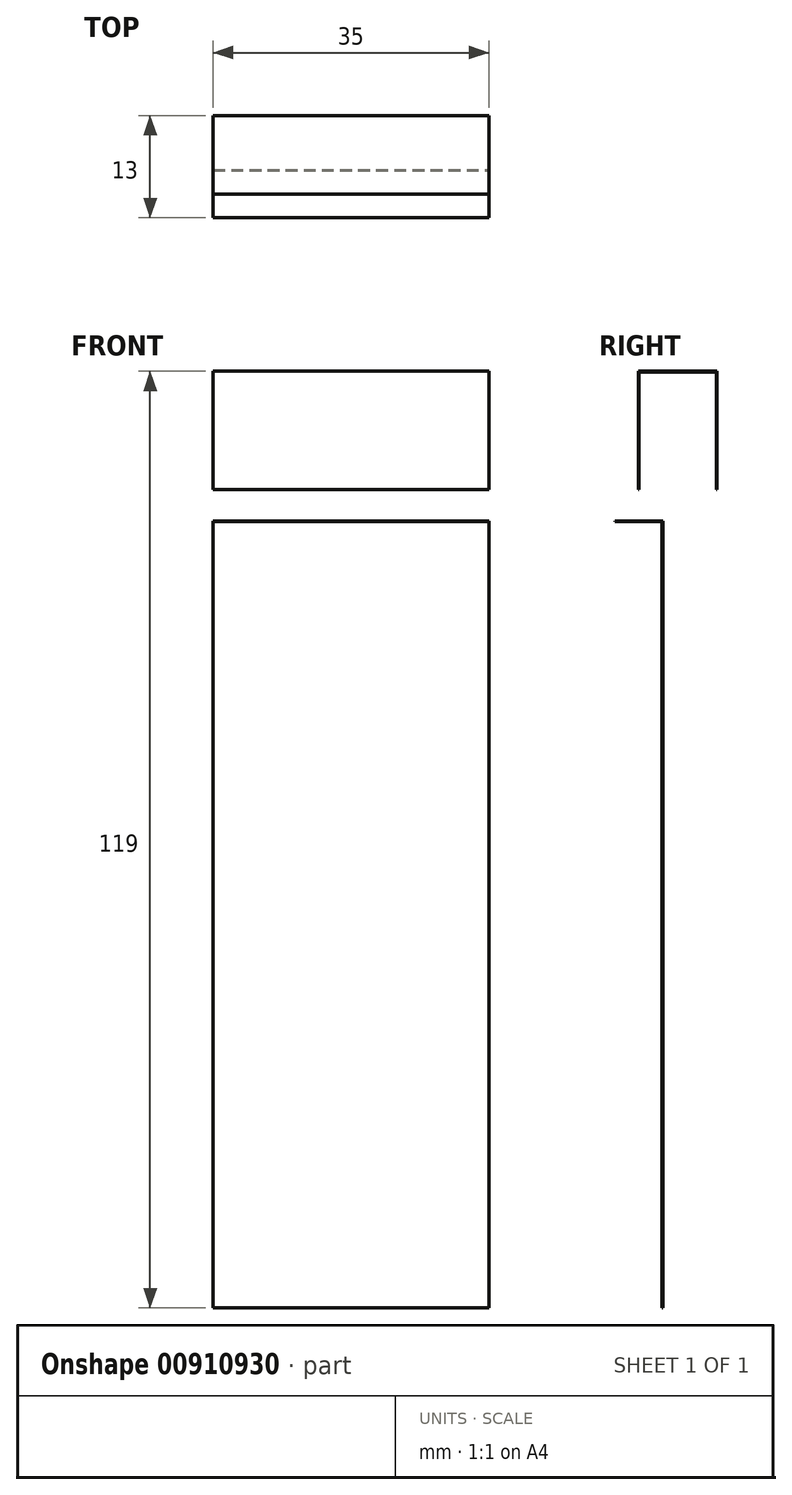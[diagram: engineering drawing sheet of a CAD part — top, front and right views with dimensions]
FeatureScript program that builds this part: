
annotation { "Feature Type Name" : "Feature", "Feature Type Description" : "" }
export const myFeature = defineFeature(function(context is Context, id is Id, definition is map)
    precondition{}
    {
        {
            assignVariable(context, id + "F0", {"name" : "D", "anyValue" : 6});
        }
        {
            assignVariable(context, id + "F1", {"name" : "w", "anyValue" : 35});
        }
        {
            var Q0;
            Q0=qCreatedBy(makeId("Top.planeOp"),FACE);
            var sketch = newSketch(context, id + "F2", { "sketchPlane" : qUnion([Q0])});
            skLineSegment(sketch, "E0.bottom", {"start": v(-17.5, 0.1) * mm, "end": v(17.5, 0.1) * mm});
            skLineSegment(sketch, "E0.top", {"start": v(-17.5, 0) * mm, "end": v(17.5, 0) * mm});
            skLineSegment(sketch, "E0.left", {"start": v(-17.5, 0.1) * mm, "end": v(-17.5, 0) * mm});
            skLineSegment(sketch, "E0.right", {"start": v(17.5, 0.1) * mm, "end": v(17.5, 0) * mm});
            skSolve(sketch);
        }
        {
            var Q0;
            Q0=makeQuery(id+"F2.imprint","IMPRINT",FACE,{"disambiguationData":[TD([[makeQuery(id+"F2.imprint","IMPRINT",EDGE,{"derivedFrom":sQuery(id+"F2.wireOp",EDGE,"E0.bottom")}),-1.0]])]});
            extrude(context, id + "F3", {"entities" : qUnion([Q0]), "oppositeDirection" : true, "depth" : 100 * mm, "offsetDistance" : 25 * mm});
        }
        {
            var Q0;
            Q0=qCreatedBy(makeId("Front.planeOp"),FACE);
            var sketch = newSketch(context, id + "F4", { "sketchPlane" : qUnion([Q0])});
            skLineSegment(sketch, "E1.bottom", {"start": v(-17.5, -0.1) * mm, "end": v(17.5, -0.1) * mm});
            skLineSegment(sketch, "E1.top", {"start": v(-17.5, 0) * mm, "end": v(17.5, 0) * mm});
            skLineSegment(sketch, "E1.left", {"start": v(-17.5, 0) * mm, "end": v(-17.5, -0.1) * mm});
            skLineSegment(sketch, "E1.right", {"start": v(17.5, 0) * mm, "end": v(17.5, -0.1) * mm});
            skSolve(sketch);
        }
        {
            var Q0;
            Q0=makeQuery(id+"F4.imprint","IMPRINT",FACE,{"disambiguationData":[TD([[makeQuery(id+"F4.imprint","IMPRINT",EDGE,{"derivedFrom":sQuery(id+"F4.wireOp",EDGE,"E1.bottom")}),1.0]])]});
            extrude(context, id + "F5", {"entities" : qUnion([Q0]), "operationType" : NewBodyOperationType.ADD, "depth" : (getVariable(context, 'D')) * mm, "offsetDistance" : 25 * mm});
        }
        {
            var Q0;
            Q0=qCreatedBy(makeId("Right.planeOp"),FACE);
            var sketch = newSketch(context, id + "F6", { "sketchPlane" : qUnion([Q0])});
            skLineSegment(sketch, "E2", {"start": v(-3, 4) * mm, "end": v(-3, 19) * mm});
            skLineSegment(sketch, "E3", {"start": v(-3, 19) * mm, "end": v(7, 19) * mm});
            skLineSegment(sketch, "E4", {"start": v(7, 19) * mm, "end": v(7, 4) * mm});
            skLineSegment(sketch, "E5", {"start": v(-3, 4) * mm, "end": v(-3, 0) * mm, "construction": true});
            skLineSegment(sketch, "E6", {"start": v(6.9, 4) * mm, "end": v(6.9, 18.9) * mm});
            skLineSegment(sketch, "E7", {"start": v(6.9, 18.9) * mm, "end": v(-2.9, 18.9) * mm});
            skLineSegment(sketch, "E8", {"start": v(-2.9, 18.9) * mm, "end": v(-2.9, 4) * mm});
            skLineSegment(sketch, "E9", {"start": v(6.9, 4) * mm, "end": v(7, 4) * mm});
            skLineSegment(sketch, "E10", {"start": v(-2.9, 4) * mm, "end": v(-3, 4) * mm});
            skSolve(sketch);
        }
        {
            var Q0;
            Q0=makeQuery(id+"F6.imprint","IMPRINT",FACE,{"disambiguationData":[TD([[makeQuery(id+"F6.imprint","IMPRINT",EDGE,{"derivedFrom":sQuery(id+"F6.wireOp",EDGE,"E2")}),-1.0]])]});
            extrude(context, id + "F7", {"entities" : qUnion([Q0]), "depth" : (getVariable(context, 'w') / 2) * mm, "offsetDistance" : 25 * mm, "hasSecondDirection" : true, "secondDirectionOppositeDirection" : true, "secondDirectionDepth" : (getVariable(context, 'w') / 2) * mm});
        }
    });
